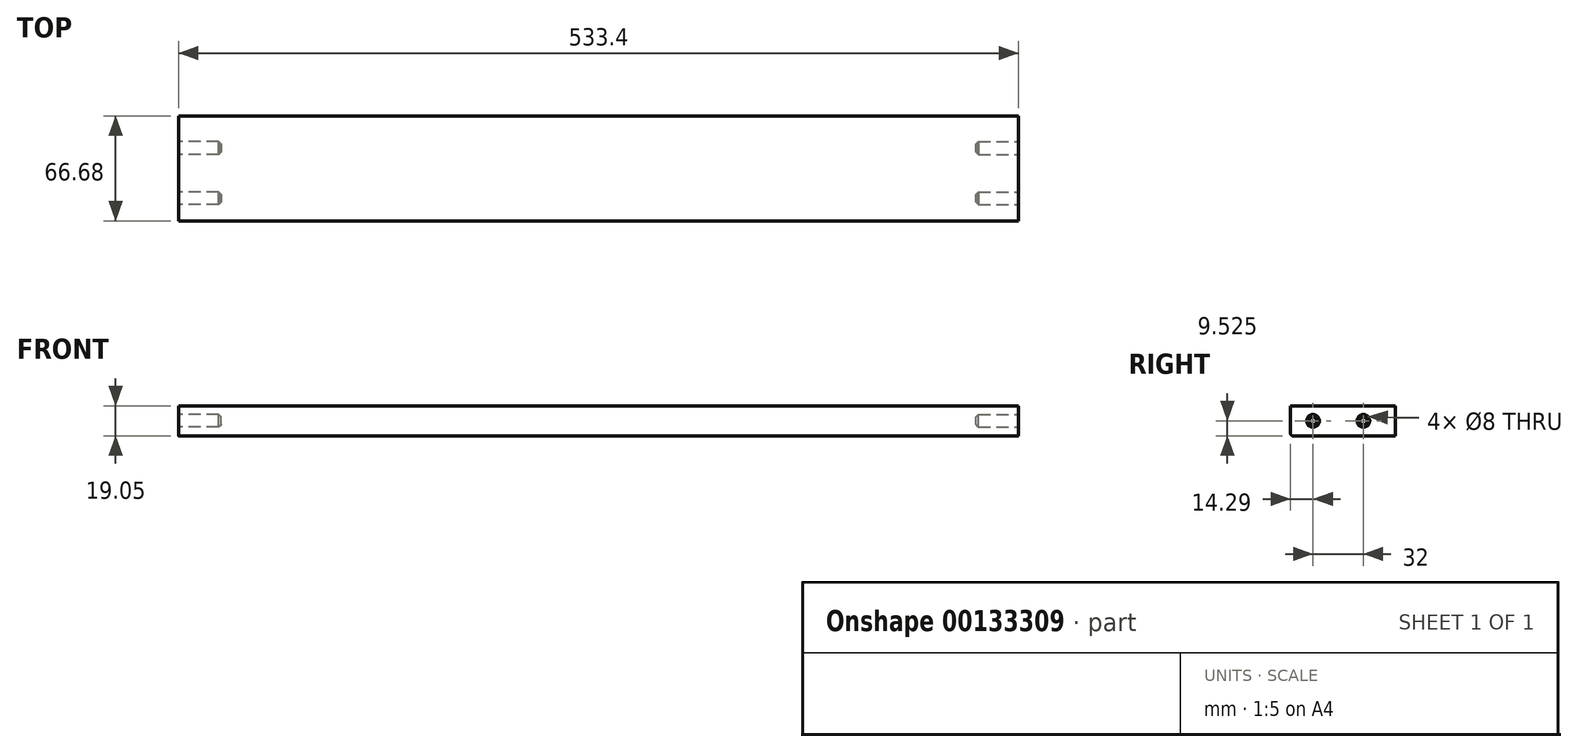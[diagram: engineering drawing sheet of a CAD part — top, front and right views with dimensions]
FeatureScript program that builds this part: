
annotation { "Feature Type Name" : "Feature", "Feature Type Description" : "" }
export const myFeature = defineFeature(function(context is Context, id is Id, definition is map)
    precondition{}
    {
        {
            var Q0;
            Q0=qCreatedBy(makeId("Top.planeOp"),FACE);
            var sketch = newSketch(context, id + "F0", { "sketchPlane" : qUnion([Q0])});
            skLineSegment(sketch, "E0.bottom", {"start": v(266.7, -33.34) * mm, "end": v(-266.7, -33.34) * mm});
            skLineSegment(sketch, "E0.top", {"start": v(266.7, 33.34) * mm, "end": v(-266.7, 33.34) * mm});
            skLineSegment(sketch, "E0.left", {"start": v(266.7, -33.34) * mm, "end": v(266.7, 33.34) * mm});
            skLineSegment(sketch, "E0.right", {"start": v(-266.7, -33.34) * mm, "end": v(-266.7, 33.34) * mm});
            skPoint(sketch, "E0.middle", {"position": v(0, 0) * mm});
            skSolve(sketch);
        }
        {
            var Q0;
            Q0=makeQuery(id+"F0.imprint","IMPRINT",FACE,{"disambiguationData":[TD([[makeQuery(id+"F0.imprint","IMPRINT",EDGE,{"derivedFrom":sQuery(id+"F0.wireOp",EDGE,"E0.bottom")}),-1.0]])]});
            extrude(context, id + "F1", {"entities" : qUnion([Q0]), "oppositeDirection" : true, "depth" : 19.05 * mm});
        }
        {
            var Q0;
            Q0=makeQuery(id+"F1.opExtrude","SWEPT_FACE",FACE,{"disambiguationData":[OSD([sQuery(id+"F0.wireOp",EDGE,"E0.left")])]});
            var sketch = newSketch(context, id + "F2", { "sketchPlane" : qUnion([Q0])});
            skPoint(sketch, "E1", {"position": v(-19.05, -9.53) * mm});
            skPoint(sketch, "E2", {"position": v(12.95, -9.53) * mm});
            skSolve(sketch);
        }
        {
            var Q0;
            Q0=qCreatedBy(makeId("Right.planeOp"),FACE);
            var sketch = newSketch(context, id + "F3", { "sketchPlane" : qUnion([Q0])});
            skCircle(sketch, "E3", {"center": v(0, 0) * mm, "radius": 4 * mm});
            skSolve(sketch);
        }
        {
            var Q0;
            Q0=makeQuery(id+"F3.imprint","IMPRINT",FACE,{"disambiguationData":[TD([[makeQuery(id+"F3.imprint","IMPRINT",EDGE,{"derivedFrom":sQuery(id+"F3.wireOp",EDGE,"E3")}),1.0]])]});
            extrude(context, id + "F4", {"entities" : qUnion([Q0]), "oppositeDirection" : true, "depth" : 26.99 * mm});
        }
        {
            var Q0;
            Q0=makeQuery(id+"F4.opExtrude","CAP_EDGE",EDGE,{"disambiguationData":[OSD([sQuery(id+"F3.wireOp",EDGE,"E3")])],"isStart":false});
            chamfer(context, id + "F5", {"entities" : qUnion([Q0]), "width" : 1.59 * mm, "tangentPropagation" : true});
        }
        {
            var Q0;
            Q0=makeQuery(id+"F4.opExtrude","SWEPT_BODY",BODY,{"disambiguationData":[OSD([sQuery(id+"F3.wireOp",EDGE,"E3")])]});
            var Q1;
            Q1=qCreatedBy(makeId("Origin.pointOp"),VERTEX);
            var Q2;
            Q2=sQuery(id+"F2.wireOp",VERTEX,"E1");
            transform(context, id + "F6", {"entities" : qUnion([Q0]), "transformType" : TransformType.TRANSLATION_ENTITY, "oppositeDirectionEntity" : false, "transformLine" : qUnion([Q1, Q2]), "makeCopy" : true});
        }
        {
            var Q0;
            Q0=makeQuery(id+"F4.opExtrude","SWEPT_BODY",BODY,{"disambiguationData":[OSD([sQuery(id+"F3.wireOp",EDGE,"E3")])]});
            var Q1;
            Q1=qCreatedBy(makeId("Origin.pointOp"),VERTEX);
            var Q2;
            Q2=sQuery(id+"F2.wireOp",VERTEX,"E2");
            transform(context, id + "F7", {"entities" : qUnion([Q0]), "transformType" : TransformType.TRANSLATION_ENTITY, "oppositeDirectionEntity" : false, "transformLine" : qUnion([Q1, Q2]), "makeCopy" : false});
        }
        {
            var Q0;
            Q0=makeQuery(id+"F4.opExtrude","SWEPT_BODY",BODY,{"disambiguationData":[OSD([sQuery(id+"F3.wireOp",EDGE,"E3")])]});
            var Q1;
            Q1=makeQuery(id+"F6.opPattern","COPY",BODY,{"derivedFrom":makeQuery(id+"F4.opExtrude","SWEPT_BODY",BODY,{"disambiguationData":[OSD([sQuery(id+"F3.wireOp",EDGE,"E3")])]}),"instanceName":"1"});
            var Q2;
            Q2=qCreatedBy(makeId("Right.planeOp"),FACE);
            mirror(context, id + "F8", {"entities" : qUnion([Q0, Q1]), "mirrorPlane" : qUnion([Q2])});
        }
        {
            var Q0;
            Q0=makeQuery(id+"F8.opPattern","COPY",BODY,{"derivedFrom":makeQuery(id+"F6.opPattern","COPY",BODY,{"derivedFrom":makeQuery(id+"F4.opExtrude","SWEPT_BODY",BODY,{"disambiguationData":[OSD([sQuery(id+"F3.wireOp",EDGE,"E3")])]}),"instanceName":"1"}),"instanceName":"1"});
            var Q1;
            Q1=makeQuery(id+"F8.opPattern","COPY",BODY,{"derivedFrom":makeQuery(id+"F4.opExtrude","SWEPT_BODY",BODY,{"disambiguationData":[OSD([sQuery(id+"F3.wireOp",EDGE,"E3")])]}),"instanceName":"1"});
            var Q2;
            Q2=makeQuery(id+"F6.opPattern","COPY",BODY,{"derivedFrom":makeQuery(id+"F4.opExtrude","SWEPT_BODY",BODY,{"disambiguationData":[OSD([sQuery(id+"F3.wireOp",EDGE,"E3")])]}),"instanceName":"1"});
            var Q3;
            Q3=makeQuery(id+"F4.opExtrude","SWEPT_BODY",BODY,{"disambiguationData":[OSD([sQuery(id+"F3.wireOp",EDGE,"E3")])]});
            var Q4;
            Q4=makeQuery(id+"F1.opExtrude","SWEPT_BODY",BODY,{"disambiguationData":[OSD([sQuery(id+"F0.wireOp",EDGE,"E0.bottom"),sQuery(id+"F0.wireOp",EDGE,"E0.top"),sQuery(id+"F0.wireOp",EDGE,"E0.left"),sQuery(id+"F0.wireOp",EDGE,"E0.right")])]});
            booleanBodies(context, id + "F9", {"operationType" : BooleanOperationType.SUBTRACTION, "tools" : qUnion([Q0, Q1, Q2, Q3]), "targets" : qUnion([Q4])});
        }
        {
            var Q0;
            Q0=makeQuery(id+"F1.opExtrude","CAP_EDGE",EDGE,{"disambiguationData":[OSD([sQuery(id+"F0.wireOp",EDGE,"E0.bottom")])],"isStart":false});
            fillet(context, id + "F10", {"entities" : qUnion([Q0]), "radius" : 1.59 * mm, "tangentPropagation" : true, "allowEdgeOverflow" : false});
        }
    });
